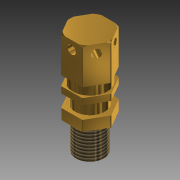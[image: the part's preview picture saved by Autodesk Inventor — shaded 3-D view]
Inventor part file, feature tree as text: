
AUTODESK INVENTOR PART (.ipt)
format: ipt  version: 2018 (Build 220112000, 112)  size: 227,840 bytes
history: native  units: mm (DEFAULTED — no unit token found)
features: sketch x9, projected_geometry x9, extrude x8, pattern_circular x1, thread x1, fillet x1, revolve x1
ambient origin geometry x8: Origin, YZ Plane, XZ Plane, XY Plane, X Axis, Y Axis, Z Axis, Center Point
bodies: Solid1 (feature_tree)
feature tree (30):
  extrude  "Extrusion1"  Depth=17.0mm TaperAngle=0.0deg
  extrude  "Extrusion2"  Depth=4.5mm TaperAngle=0.0deg
  extrude  "Extrusion3"  Depth=14.0mm
  extrude  "Extrusion4"  Depth=5.0mm TaperAngle=0.0deg
  extrude  "Extrusion5"  Depth=14.5mm TaperAngle=0.0deg
  extrude  "Extrusion6"  Depth=47.5mm TaperAngle=0.0deg
  extrude  "Extrusion7"  Depth=4.0mm
  extrude  "Extrusion8"  Depth=30.0mm TaperAngle=360.0deg
  pattern_circular  "Circular Pattern1"  Angle=45.0deg  [1 undecoded]
  thread  "Thread1"  [1 undecoded]
  fillet  "Fillet1"  [1 undecoded]
  revolve  "Revolution2"  [1 undecoded]
  sketch  "Sketch1"  dims[d0=17.5mm d1=17.0mm d2=0.0mm]
  sketch  "Sketch2"  dims[d3=16.5mm d4=4.5mm d5=0.0mm]
  projected_geometry  "Projected Loop1"
  sketch  "Sketch3"  dims[d6=3.0mm d7=0.0mm d8=14.0mm]
  projected_geometry  "Projected Loop2"
  sketch  "Sketch4"  dims[d9=6.0mm d10=0.0mm d11=5.0mm d12=0.0mm]
  projected_geometry  "Projected Loop3"
  sketch  "Sketch5"  dims[d13=13.25mm d14=14.5mm d15=0.0mm]
  projected_geometry  "Projected Loop4"
  sketch  "Sketch6"  dims[d16=5.0mm d17=47.5mm d18=0.0mm]
  projected_geometry  "Projected Loop5"
  sketch  "Sketch7"  dims[d19=4.0mm d20=4.0mm]
  projected_geometry  "Projected Loop6"
  sketch  "Sketch8"  dims[d21=40.25mm d22=0.0mm d23=30.0mm d25=360.0deg]
  projected_geometry  "Projected Loop7"
  sketch  "Sketch10"  dims[d26=10.0mm d27=0.0mm d28=0.5mm d32=45.0deg d33=1.0mm d34=90.0deg]
  projected_geometry  "Projected Loop8"
  projected_geometry  "Projected Loop9"
note: 4 required parameter values undecoded (feature->parameter linkage not recoverable at this tier; creation-order binding heuristic only, values carry confidence <= 0.55)
